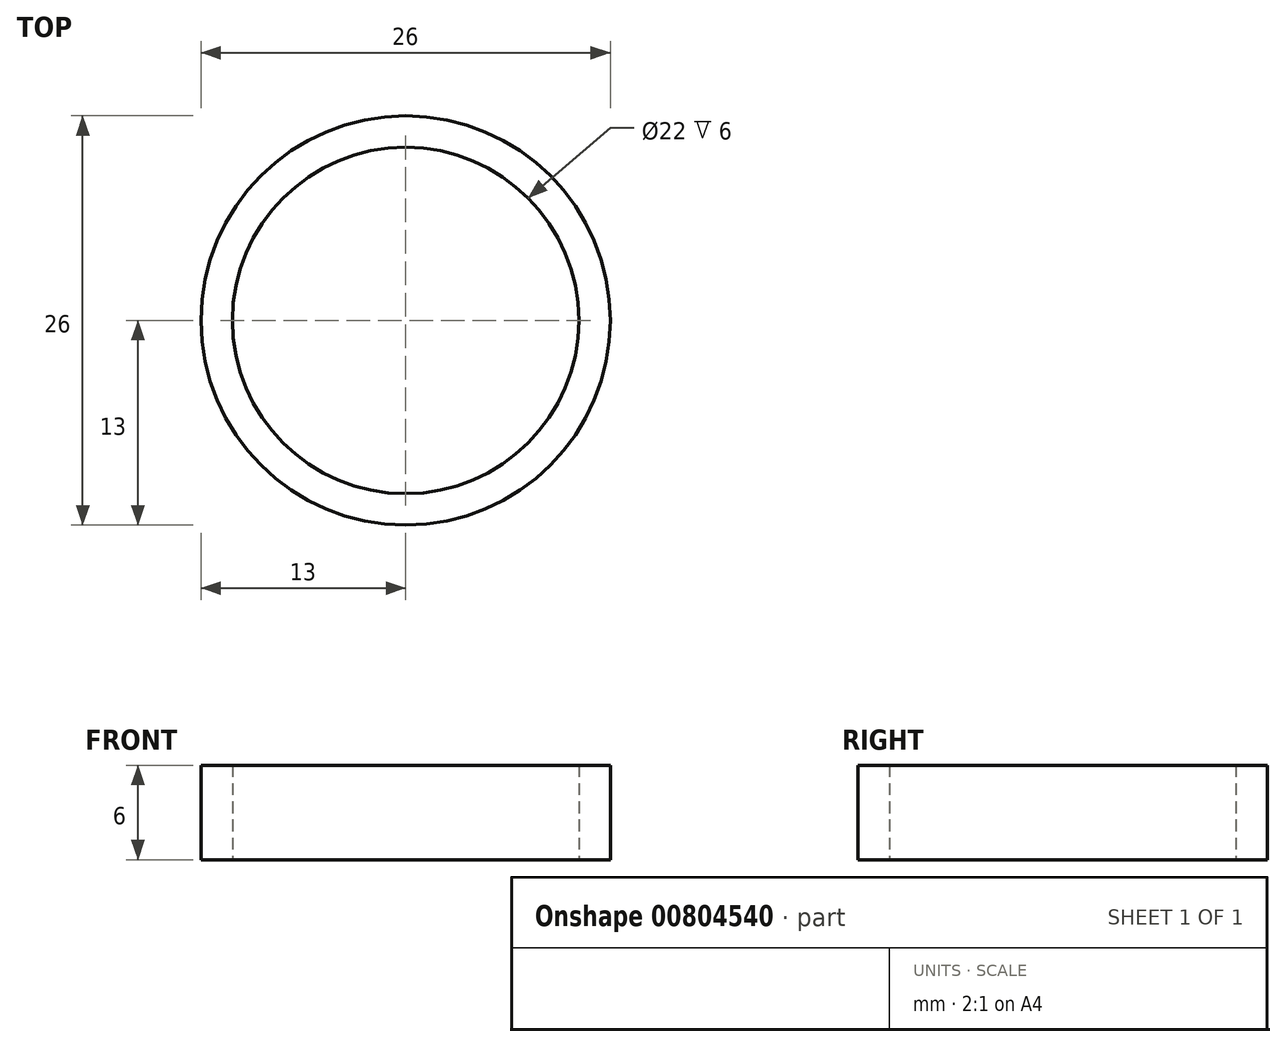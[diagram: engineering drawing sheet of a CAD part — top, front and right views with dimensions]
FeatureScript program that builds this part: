
annotation { "Feature Type Name" : "Feature", "Feature Type Description" : "" }
export const myFeature = defineFeature(function(context is Context, id is Id, definition is map)
    precondition{}
    {
        {
            var Q0;
            Q0=qCreatedBy(makeId("Top.planeOp"),FACE);
            var sketch = newSketch(context, id + "F0", { "sketchPlane" : qUnion([Q0])});
            skCircle(sketch, "E0", {"center": v(0, 0) * mm, "radius": 11 * mm});
            skCircle(sketch, "E1", {"center": v(0, 0) * mm, "radius": 13 * mm});
            skSolve(sketch);
        }
        {
            var Q0;
            Q0=makeQuery(id+"F0.imprint","IMPRINT",FACE,{"disambiguationData":[TD([[makeQuery(id+"F0.imprint","IMPRINT",EDGE,{"derivedFrom":sQuery(id+"F0.wireOp",EDGE,"E0")}),-1.0]])]});
            extrude(context, id + "F1", {"entities" : qUnion([Q0]), "depth" : 6 * mm, "offsetDistance" : 25 * mm});
        }
    });
